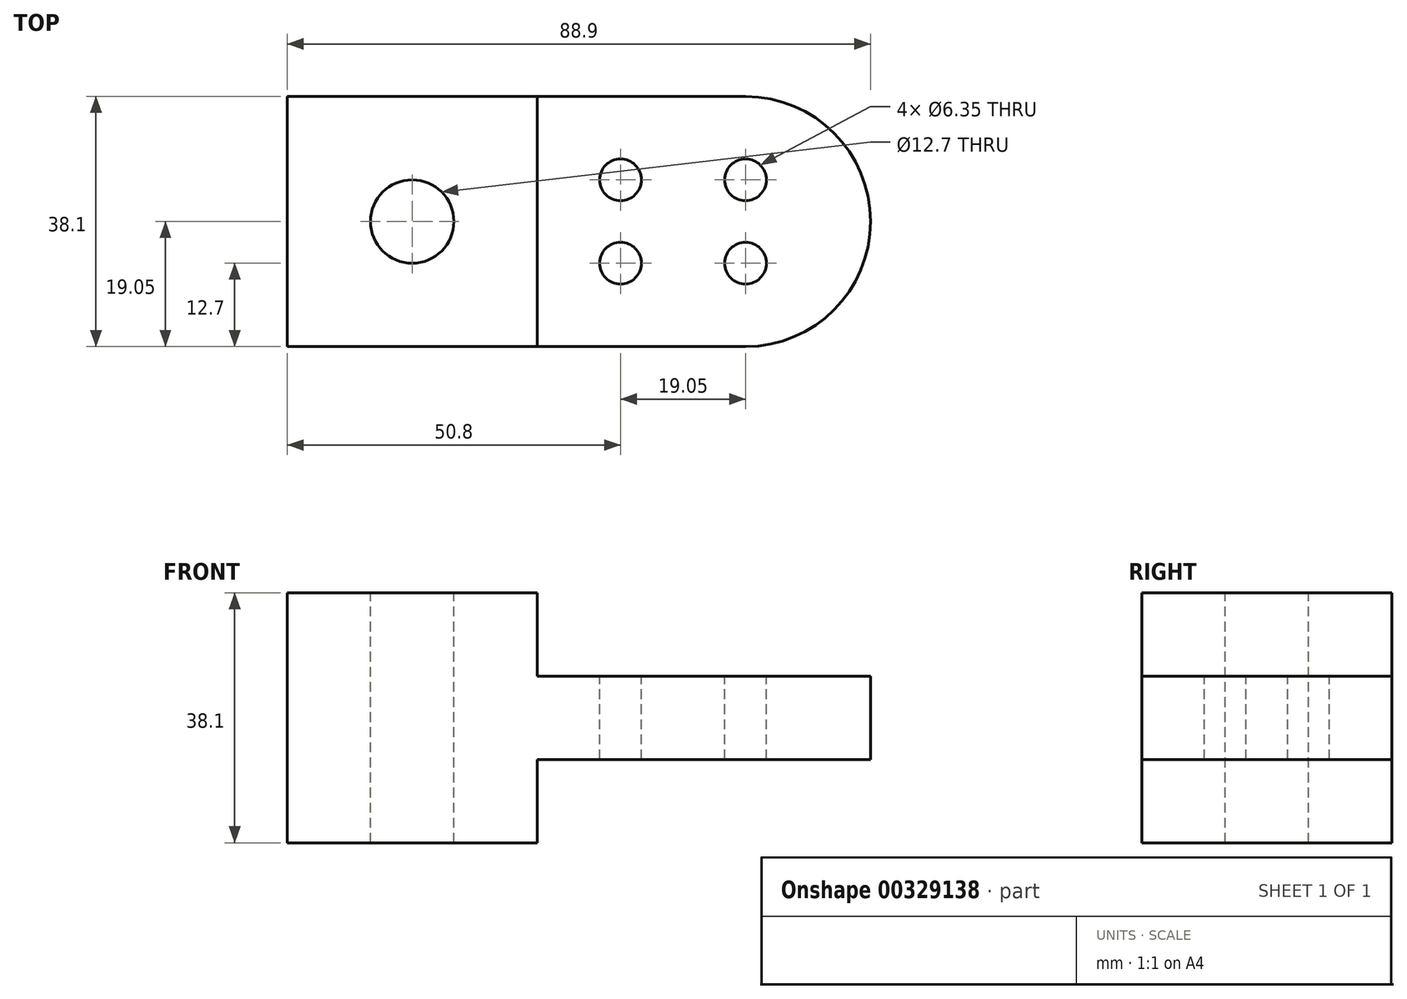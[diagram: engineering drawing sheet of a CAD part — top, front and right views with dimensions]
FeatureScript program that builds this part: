
annotation { "Feature Type Name" : "Feature", "Feature Type Description" : "" }
export const myFeature = defineFeature(function(context is Context, id is Id, definition is map)
    precondition{}
    {
        {
            var Q0;
            Q0=qCreatedBy(makeId("Front.planeOp"),FACE);
            var sketch = newSketch(context, id + "F0", { "sketchPlane" : qUnion([Q0])});
            skLineSegment(sketch, "E0", {"start": v(0, 0) * mm, "end": v(0, 38.1) * mm});
            skLineSegment(sketch, "E1", {"start": v(38.1, 38.1) * mm, "end": v(38.1, 25.4) * mm});
            skLineSegment(sketch, "E2", {"start": v(38.1, 25.4) * mm, "end": v(88.9, 25.4) * mm});
            skLineSegment(sketch, "E3", {"start": v(88.9, 25.4) * mm, "end": v(88.9, 12.7) * mm});
            skLineSegment(sketch, "E4", {"start": v(88.9, 12.7) * mm, "end": v(38.1, 12.7) * mm});
            skLineSegment(sketch, "E5", {"start": v(38.1, 12.7) * mm, "end": v(38.1, 0) * mm});
            skLineSegment(sketch, "E6", {"start": v(38.1, 0) * mm, "end": v(0, 0) * mm});
            skLineSegment(sketch, "E7", {"start": v(0, 38.1) * mm, "end": v(38.1, 38.1) * mm});
            skLineSegment(sketch, "E8", {"start": v(0, 38.1) * mm, "end": v(0, 0) * mm});
            skLineSegment(sketch, "E9", {"start": v(0, 0) * mm, "end": v(38.1, 0) * mm});
            skSolve(sketch);
        }
        {
            var Q0;
            Q0=makeQuery(id+"F0.imprint","IMPRINT",FACE,{"disambiguationData":[TD([[makeQuery(id+"F0.imprint","IMPRINT",EDGE,{"derivedFrom":sQuery(id+"F0.wireOp",EDGE,"E1")}),-1.0]])]});
            extrude(context, id + "F1", {"entities" : qUnion([Q0]), "depth" : 38.1 * mm});
        }
        {
            var Q0;
            Q0=makeQuery(id+"F1.opExtrude","CAP_EDGE",EDGE,{"disambiguationData":[OSD([sQuery(id+"F0.wireOp",EDGE,"E3")])],"isStart":true});
            var Q1;
            Q1=makeQuery(id+"F1.opExtrude","CAP_EDGE",EDGE,{"disambiguationData":[OSD([sQuery(id+"F0.wireOp",EDGE,"E3")])],"isStart":false});
            fillet(context, id + "F2", {"entities" : qUnion([Q0, Q1]), "radius" : 19.05 * mm, "tangentPropagation" : true, "allowEdgeOverflow" : false});
        }
        {
            var Q0;
            Q0=makeQuery(id+"F1.opExtrude","SWEPT_FACE",FACE,{"disambiguationData":[OSD([sQuery(id+"F0.wireOp",EDGE,"E7")])]});
            var sketch = newSketch(context, id + "F3", { "sketchPlane" : qUnion([Q0])});
            skCircle(sketch, "E10", {"center": v(19.05, -19.05) * mm, "radius": 6.35 * mm});
            skSolve(sketch);
        }
        {
            var Q0;
            Q0=makeQuery(id+"F1.opExtrude","SWEPT_FACE",FACE,{"disambiguationData":[OSD([sQuery(id+"F0.wireOp",EDGE,"E2")])]});
            var sketch = newSketch(context, id + "F4", { "sketchPlane" : qUnion([Q0])});
            skCircle(sketch, "E11", {"center": v(50.8, -25.4) * mm, "radius": 3.18 * mm});
            skCircle(sketch, "E12", {"center": v(50.8, -12.7) * mm, "radius": 3.18 * mm});
            skCircle(sketch, "E13", {"center": v(69.85, -25.4) * mm, "radius": 3.18 * mm});
            skCircle(sketch, "E14", {"center": v(69.85, -12.7) * mm, "radius": 3.18 * mm});
            skSolve(sketch);
        }
        {
            var Q0;
            Q0=makeQuery(id+"F3.imprint","IMPRINT",FACE,{"disambiguationData":[TD([[makeQuery(id+"F3.imprint","IMPRINT",EDGE,{"derivedFrom":sQuery(id+"F3.wireOp",EDGE,"E10")}),1.0]])]});
            extrude(context, id + "F5", {"entities" : qUnion([Q0]), "operationType" : NewBodyOperationType.REMOVE, "endBound" : BoundingType.THROUGH_ALL, "oppositeDirection" : true, "depth" : 25.4 * mm});
        }
        {
            var Q0;
            Q0=makeQuery(id+"F4.imprint","IMPRINT",FACE,{"disambiguationData":[TD([[makeQuery(id+"F4.imprint","IMPRINT",EDGE,{"derivedFrom":sQuery(id+"F4.wireOp",EDGE,"E13")}),1.0]])]});
            var Q1;
            Q1=makeQuery(id+"F4.imprint","IMPRINT",FACE,{"disambiguationData":[TD([[makeQuery(id+"F4.imprint","IMPRINT",EDGE,{"derivedFrom":sQuery(id+"F4.wireOp",EDGE,"E14")}),1.0]])]});
            var Q2;
            Q2=makeQuery(id+"F4.imprint","IMPRINT",FACE,{"disambiguationData":[TD([[makeQuery(id+"F4.imprint","IMPRINT",EDGE,{"derivedFrom":sQuery(id+"F4.wireOp",EDGE,"E12")}),1.0]])]});
            var Q3;
            Q3=makeQuery(id+"F4.imprint","IMPRINT",FACE,{"disambiguationData":[TD([[makeQuery(id+"F4.imprint","IMPRINT",EDGE,{"derivedFrom":sQuery(id+"F4.wireOp",EDGE,"E11")}),1.0]])]});
            extrude(context, id + "F6", {"entities" : qUnion([Q0, Q1, Q2, Q3]), "operationType" : NewBodyOperationType.REMOVE, "endBound" : BoundingType.THROUGH_ALL, "oppositeDirection" : true, "depth" : 25.4 * mm});
        }
    });
